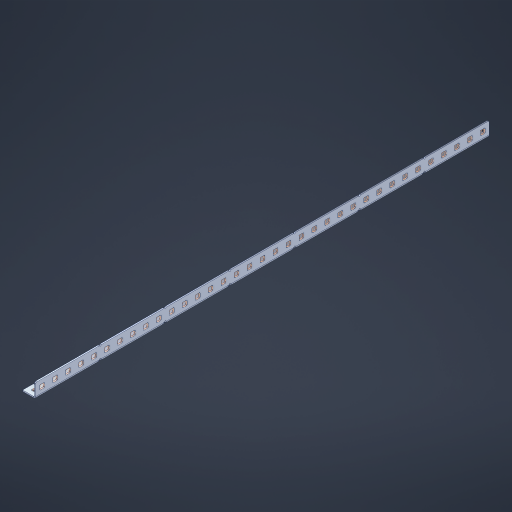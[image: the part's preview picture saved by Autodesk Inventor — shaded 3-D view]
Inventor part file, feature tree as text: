
AUTODESK INVENTOR PART (.ipt)
format: ipt  version: 2023 (Build 270158000, 158)  size: 1,331,200 bytes
history: native  units: in
note: dims shown in document units (in); Inventor stores cm internally (conversion verified against a paired STEP export)
features: other x111, extrude x102, sheet_metal_op x11, sketch x10, pattern_linear x2, mirror x1, chamfer x1
ambient origin geometry x8: Origin, YZ Plane, XZ Plane, XY Plane, X Axis, Y Axis, Z Axis, Center Point
bodies: Solid1 (feature_tree), Body (feature_tree)
feature tree (238):
  sheet_metal_op  "Flanges"
  other  "Flange Pattern Plane"
  other  "Flange Pattern Sketch"
  sheet_metal_op  "Flange Pattern"
  sheet_metal_op  "Body Pattern"
  pattern_linear  "Center Pattern"  Spacing1=0.0469in  [1 undecoded]
  other  "Arc Length"
  mirror  "Notch Mirror"
  pattern_linear  "Notch Pattern"  Spacing1=0.182in  [1 undecoded]
  chamfer  "End Chamfer"
  extrude  "Half Cut"  Depth=0.02in
  sketch  "Sketch1"  dims[d0=1.0in]
  other  "Plate1"
  sketch  "Sketch2"  dims[d1=17.5in]
  other  "Plate2"
  sheet_metal_op  "Bend1"
  sheet_metal_op  "Corner1"
  sketch  "Sketch3"  dims[d2=0.0469in]
  sketch  "Sketch7"  dims[d3=0.0469in]
  other  "Srf1"
  other  "Srf2"
  sketch  "Sketch8"  dims[d4=0.0234in]
  sketch  "Sketch9"  dims[d5=0.0938in]
  other  "Srf91"
  sheet_metal_op  "Body Pattern Sketch"
  other  "Srf92"
  sketch  "Sketch13"  dims[d6=0.0469in]
  sketch  "Sketch14"  dims[d7=0.5in d8=90.0deg d9=0.0312in]
  sketch  "Sketch15"  dims[d10=0.1875in]
  sketch  "Sketch16"  dims[d11=0.0469in d12=0.0469in d16=0.182in d17=0.02in d18=0.0469in d19=0.0in d20=0.25in d21=0.25in d38=13.7795in d40=0.5in d41=0.3937in d43=1.0in d46=0.172in d47=1.0in d48=0.0in d49=0.182in d50=0.02in d51=0.25in d52=0.25in d53=0.0469in d54=0.0in d55=0.172in d56=1.0in d57=0.0in d58=0.25in d60=13.7795in d62=0.5in d63=0.3937in d65=0.5in d85=0.1227in d86=0.1659in d88=0.04in d89=0.0469in d90=0.0in d91=0.04in d92=0.0491in d95=2.5in d96=0.04in d97=0.25in d98=45.0deg d99=0.25in d100=0.5in d101=0.0in d102=2.497in d106=0.182in d107=0.02in d108=0.5in d109=0.5in d110=0.0469in d111=0.0in d112=0.172in d113=0.5in d114=0.0in d117=0.5in d118=0.5in d119=0.5in]
  other  "Srf786"
  other  "Srf823"
  other  "Srf824"
  other  "Srf825"
  other  "Srf826"
  other  "Srf827"
  other  "Srf828"
  other  "Srf829"
  other  "Srf856"
  other  "Srf857"
  other  "Srf858"
  other  "Srf859"
  other  "Srf860"
  other  "Srf861"
  other  "Srf862"
  other  "Srf889"
  other  "Srf890"
  other  "Srf891"
  other  "Srf892"
  other  "Srf893"
  other  "Srf894"
  other  "Srf895"
  other  "Srf896"
  other  "Srf1275"
  other  "Srf1276"
  other  "Srf1277"
  other  "Srf1278"
  other  "Srf1279"
  other  "Srf1280"
  other  "Srf1281"
  other  "Srf1282"
  other  "Srf1283"
  other  "Srf1284"
  other  "Srf1285"
  other  "Srf1286"
  other  "Srf1287"
  other  "Srf1288"
  other  "Srf1289"
  other  "Srf1290"
  other  "Srf1291"
  other  "Srf1292"
  other  "Srf1293"
  other  "Srf1294"
  other  "Srf1295"
  other  "Srf1296"
  other  "Srf1297"
  other  "Srf1298"
  other  "Srf1299"
  other  "Srf1300"
  other  "Srf1301"
  other  "Srf1302"
  other  "Srf1303"
  other  "Srf1304"
  other  "Srf1305"
  other  "Srf1306"
  other  "Srf1307"
  other  "Srf1308"
  other  "Srf1309"
  other  "Srf1310"
  other  "Srf1311"
  other  "Srf1312"
  other  "Srf1313"
  other  "Srf1314"
  other  "Srf1315"
  other  "Srf1316"
  other  "Srf1317"
  other  "Srf1318"
  other  "Srf1319"
  other  "Srf1320"
  other  "Srf1321"
  other  "Srf1322"
  other  "Srf1323"
  other  "Srf1324"
  other  "Srf1325"
  other  "Srf1326"
  other  "Srf1327"
  other  "Srf1328"
  other  "Srf1329"
  other  "Srf1330"
  other  "Srf1331"
  other  "Srf1332"
  other  "Srf1333"
  other  "Srf1334"
  other  "Srf1335"
  other  "Srf1336"
  other  "Srf1337"
  other  "Srf1338"
  other  "Srf1339"
  other  "Srf1340"
  other  "Srf1341"
  other  "Srf1342"
  other  "Srf1343"
  other  "Srf1344"
  other  "Srf1345"
  other  "Srf1346"
  other  "Srf1347"
  other  "Srf1348"
  other  "Srf1349"
  other  "Srf1350"
  other  "Srf1351"
  sheet_metal_op  "Flange Stamp"
  sheet_metal_op  "Flange Circle"
  sheet_metal_op  "Body Stamp"
  sheet_metal_op  "Body Circle"
  other  "Center Stamp"
  other  "Center Circle"
  sheet_metal_op  "Notch"
  extrude  "ExtrusionSrf2"  Depth=0.0469in
  extrude  "ExtrusionSrf92"  TaperAngle=0.0deg  [1 undecoded]
  extrude  "ExtrusionSrf823"  Depth=0.25in
  extrude  "ExtrusionSrf824"  Depth=0.25in
  extrude  "ExtrusionSrf825"  Depth=0.5in
  extrude  "ExtrusionSrf826"  Depth=0.5in
  extrude  "ExtrusionSrf827"  Depth=1.0in TaperAngle=0.0deg
  extrude  "ExtrusionSrf828"  Depth=0.182in
  extrude  "ExtrusionSrf829"  Depth=0.02in
  extrude  "ExtrusionSrf856"  Depth=0.25in
  extrude  "ExtrusionSrf857"  Depth=0.25in
  extrude  "ExtrusionSrf858"  Depth=0.0469in
  extrude  "ExtrusionSrf859"  TaperAngle=0.0deg  [1 undecoded]
  extrude  "ExtrusionSrf860"  Depth=0.5in
  extrude  "ExtrusionSrf861"  Depth=1.0in TaperAngle=0.0deg
  extrude  "ExtrusionSrf862"  Depth=0.25in
  extrude  "ExtrusionSrf889"  Depth=0.5in
  extrude  "ExtrusionSrf890"  Depth=0.5in
  extrude  "ExtrusionSrf891"  Depth=0.5in
  extrude  "ExtrusionSrf892"  Depth=0.5in
  extrude  "ExtrusionSrf893"  Depth=0.5in
  extrude  "ExtrusionSrf894"  Depth=0.0469in
  extrude  "ExtrusionSrf895"  TaperAngle=0.0deg  [1 undecoded]
  extrude  "ExtrusionSrf896"  Depth=0.5in
  extrude  "ExtrusionSrf1275"  Depth=0.5in
  extrude  "ExtrusionSrf1276"  Depth=2.5in
  extrude  "ExtrusionSrf1277"  Depth=0.25in TaperAngle=45.0deg
  extrude  "ExtrusionSrf1278"  Depth=0.25in
  extrude  "ExtrusionSrf1279"  Depth=0.5in TaperAngle=0.0deg
  extrude  "ExtrusionSrf1280"  Depth=0.5in
  extrude  "ExtrusionSrf1281"  Depth=0.182in
  extrude  "ExtrusionSrf1282"  Depth=0.02in
  extrude  "ExtrusionSrf1283"  Depth=0.5in
  extrude  "ExtrusionSrf1284"  Depth=0.5in
  extrude  "ExtrusionSrf1285"  Depth=0.0469in
  extrude  "ExtrusionSrf1286"  TaperAngle=0.0deg  [1 undecoded]
  extrude  "ExtrusionSrf1287"  Depth=0.5in
  extrude  "ExtrusionSrf1288"  Depth=0.5in TaperAngle=0.0deg
  extrude  "ExtrusionSrf1289"  Depth=0.5in
  extrude  "ExtrusionSrf1290"  Depth=0.5in
  extrude  "ExtrusionSrf1291"  Depth=0.5in
  extrude  "ExtrusionSrf1292"  [1 undecoded]
  extrude  "ExtrusionSrf1293"  [1 undecoded]
  extrude  "ExtrusionSrf1294"  [1 undecoded]
  extrude  "ExtrusionSrf1295"  [1 undecoded]
  extrude  "ExtrusionSrf1296"  [1 undecoded]
  extrude  "ExtrusionSrf1297"  [1 undecoded]
  extrude  "ExtrusionSrf1298"  [1 undecoded]
  extrude  "ExtrusionSrf1299"  [1 undecoded]
  extrude  "ExtrusionSrf1300"  [1 undecoded]
  extrude  "ExtrusionSrf1301"  [1 undecoded]
  extrude  "ExtrusionSrf1302"  [1 undecoded]
  extrude  "ExtrusionSrf1303"  [1 undecoded]
  extrude  "ExtrusionSrf1304"  [1 undecoded]
  extrude  "ExtrusionSrf1305"  [1 undecoded]
  extrude  "ExtrusionSrf1306"  [1 undecoded]
  extrude  "ExtrusionSrf1307"  [1 undecoded]
  extrude  "ExtrusionSrf1308"  [1 undecoded]
  extrude  "ExtrusionSrf1309"  [1 undecoded]
  extrude  "ExtrusionSrf1310"  [1 undecoded]
  extrude  "ExtrusionSrf1311"  [1 undecoded]
  extrude  "ExtrusionSrf1312"  [1 undecoded]
  extrude  "ExtrusionSrf1313"  [1 undecoded]
  extrude  "ExtrusionSrf1314"  [1 undecoded]
  extrude  "ExtrusionSrf1315"  [1 undecoded]
  extrude  "ExtrusionSrf1316"  [1 undecoded]
  extrude  "ExtrusionSrf1317"  [1 undecoded]
  extrude  "ExtrusionSrf1318"  [1 undecoded]
  extrude  "ExtrusionSrf1319"  [1 undecoded]
  extrude  "ExtrusionSrf1320"  [1 undecoded]
  extrude  "ExtrusionSrf1321"  [1 undecoded]
  extrude  "ExtrusionSrf1322"  [1 undecoded]
  extrude  "ExtrusionSrf1323"  [1 undecoded]
  extrude  "ExtrusionSrf1324"  [1 undecoded]
  extrude  "ExtrusionSrf1325"  [1 undecoded]
  extrude  "ExtrusionSrf1326"  [1 undecoded]
  extrude  "ExtrusionSrf1327"  [1 undecoded]
  extrude  "ExtrusionSrf1328"  [1 undecoded]
  extrude  "ExtrusionSrf1329"  [1 undecoded]
  extrude  "ExtrusionSrf1330"  [1 undecoded]
  extrude  "ExtrusionSrf1331"  [1 undecoded]
  extrude  "ExtrusionSrf1332"  [1 undecoded]
  extrude  "ExtrusionSrf1333"  [1 undecoded]
  extrude  "ExtrusionSrf1334"  [1 undecoded]
  extrude  "ExtrusionSrf1335"  [1 undecoded]
  extrude  "ExtrusionSrf1336"  [1 undecoded]
  extrude  "ExtrusionSrf1337"  [1 undecoded]
  extrude  "ExtrusionSrf1338"  [1 undecoded]
  extrude  "ExtrusionSrf1339"  [1 undecoded]
  extrude  "ExtrusionSrf1340"  [1 undecoded]
  extrude  "ExtrusionSrf1341"  [1 undecoded]
  extrude  "ExtrusionSrf1342"  [1 undecoded]
  extrude  "ExtrusionSrf1343"  [1 undecoded]
  extrude  "ExtrusionSrf1344"  [1 undecoded]
  extrude  "ExtrusionSrf1345"  [1 undecoded]
  extrude  "ExtrusionSrf1346"  [1 undecoded]
  extrude  "ExtrusionSrf1347"  [1 undecoded]
  extrude  "ExtrusionSrf1348"  [1 undecoded]
  extrude  "ExtrusionSrf1349"  [1 undecoded]
  extrude  "ExtrusionSrf1350"  [1 undecoded]
  extrude  "ExtrusionSrf1351"  [1 undecoded]
note: 66 required parameter values undecoded (feature->parameter linkage not recoverable at this tier; creation-order binding heuristic only, values carry confidence <= 0.55)
